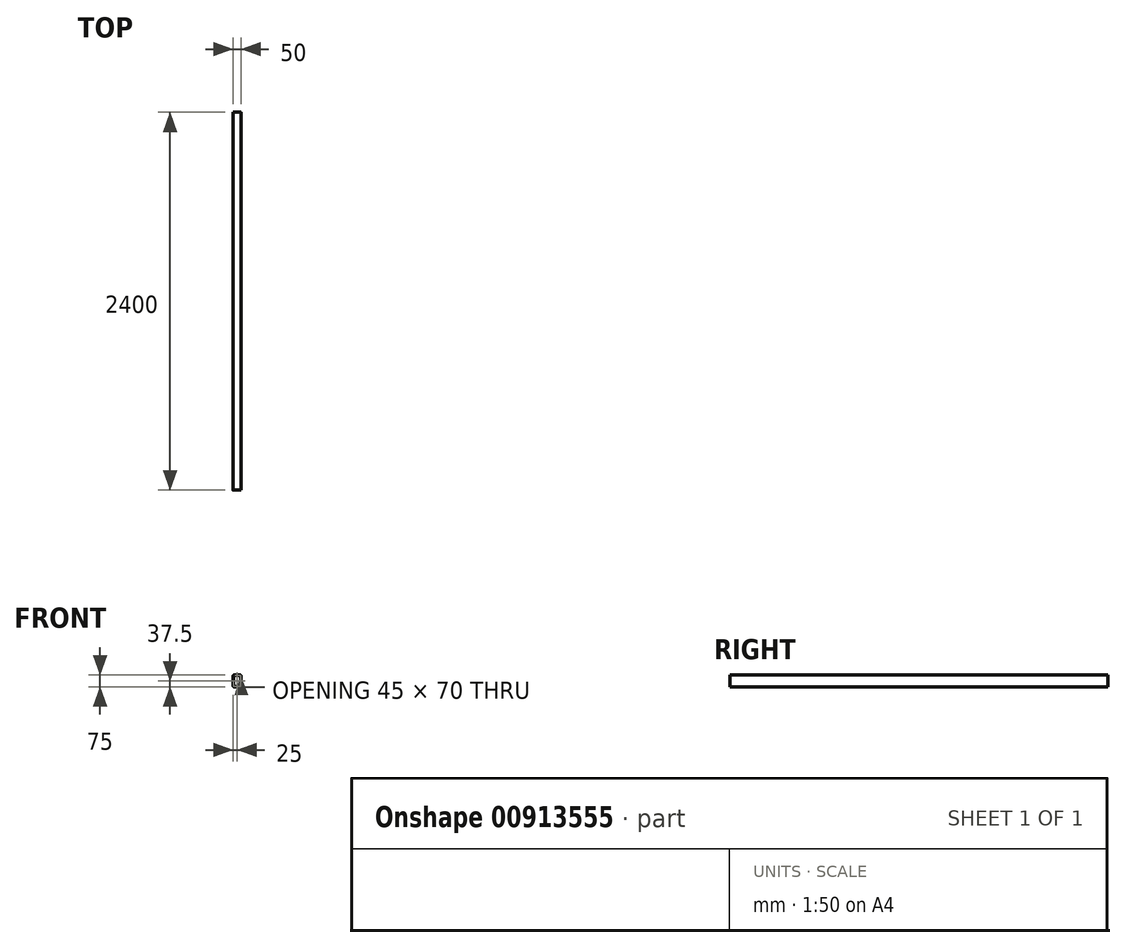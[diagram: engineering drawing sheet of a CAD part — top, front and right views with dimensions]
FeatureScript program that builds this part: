
annotation { "Feature Type Name" : "Feature", "Feature Type Description" : "" }
export const myFeature = defineFeature(function(context is Context, id is Id, definition is map)
    precondition{}
    {
        {
            var Q0;
            Q0=qCreatedBy(makeId("Front.planeOp"),FACE);
            var sketch = newSketch(context, id + "F0", { "sketchPlane" : qUnion([Q0])});
            skLineSegment(sketch, "E0.bottom", {"start": v(-25, 37.5) * mm, "end": v(25, 37.5) * mm});
            skLineSegment(sketch, "E0.left", {"start": v(-25, 37.5) * mm, "end": v(-25, -37.5) * mm});
            skLineSegment(sketch, "E1", {"start": v(-25, -37.5) * mm, "end": v(25, -37.5) * mm});
            skLineSegment(sketch, "E2", {"start": v(25, -37.5) * mm, "end": v(25, 37.5) * mm});
            skSolve(sketch);
        }
        {
            var Q0;
            Q0=makeQuery(id+"F0.imprint","IMPRINT",FACE,{"disambiguationData":[TD([[makeQuery(id+"F0.imprint","IMPRINT",EDGE,{"derivedFrom":sQuery(id+"F0.wireOp",EDGE,"E0.bottom")}),-1.0]])]});
            extrude(context, id + "F1", {"entities" : qUnion([Q0]), "endBound" : BoundingType.SYMMETRIC, "depth" : 2400 * mm, "offsetDistance" : 25 * mm});
        }
        {
            var Q0;
            Q0=makeQuery(id+"F1.opExtrude","SWEPT_EDGE",EDGE,{"disambiguationData":[OSD([sQuery(id+"F0.wireOp",EDGE,"E0.bottom"),sQuery(id+"F0.wireOp",EDGE,"E2")])]});
            var Q1;
            Q1=makeQuery(id+"F1.opExtrude","SWEPT_EDGE",EDGE,{"disambiguationData":[OSD([sQuery(id+"F0.wireOp",EDGE,"E0.bottom"),sQuery(id+"F0.wireOp",EDGE,"E0.left")])]});
            var Q2;
            Q2=makeQuery(id+"F1.opExtrude","SWEPT_EDGE",EDGE,{"disambiguationData":[OSD([sQuery(id+"F0.wireOp",EDGE,"E0.left"),sQuery(id+"F0.wireOp",EDGE,"E1")])]});
            var Q3;
            Q3=makeQuery(id+"F1.opExtrude","SWEPT_EDGE",EDGE,{"disambiguationData":[OSD([sQuery(id+"F0.wireOp",EDGE,"E1"),sQuery(id+"F0.wireOp",EDGE,"E2")])]});
            fillet(context, id + "F2", {"entities" : qUnion([Q0, Q1, Q2, Q3]), "radius" : 5.5 * mm, "tangentPropagation" : true, "allowEdgeOverflow" : false});
        }
        {
            var Q0;
            Q0=makeQuery(id+"F1.opExtrude","CAP_FACE",FACE,{"disambiguationData":[OSD([sQuery(id+"F0.wireOp",EDGE,"E0.bottom"),sQuery(id+"F0.wireOp",EDGE,"E0.left"),sQuery(id+"F0.wireOp",EDGE,"E1"),sQuery(id+"F0.wireOp",EDGE,"E2")])],"isStart":false});
            var Q1;
            Q1=makeQuery(id+"F1.opExtrude","CAP_FACE",FACE,{"disambiguationData":[OSD([sQuery(id+"F0.wireOp",EDGE,"E0.bottom"),sQuery(id+"F0.wireOp",EDGE,"E0.left"),sQuery(id+"F0.wireOp",EDGE,"E1"),sQuery(id+"F0.wireOp",EDGE,"E2")])],"isStart":true});
            shell(context, id + "F3", {"entities" : qUnion([Q0, Q1]), "thickness" : 2.5 * mm});
        }
    });
